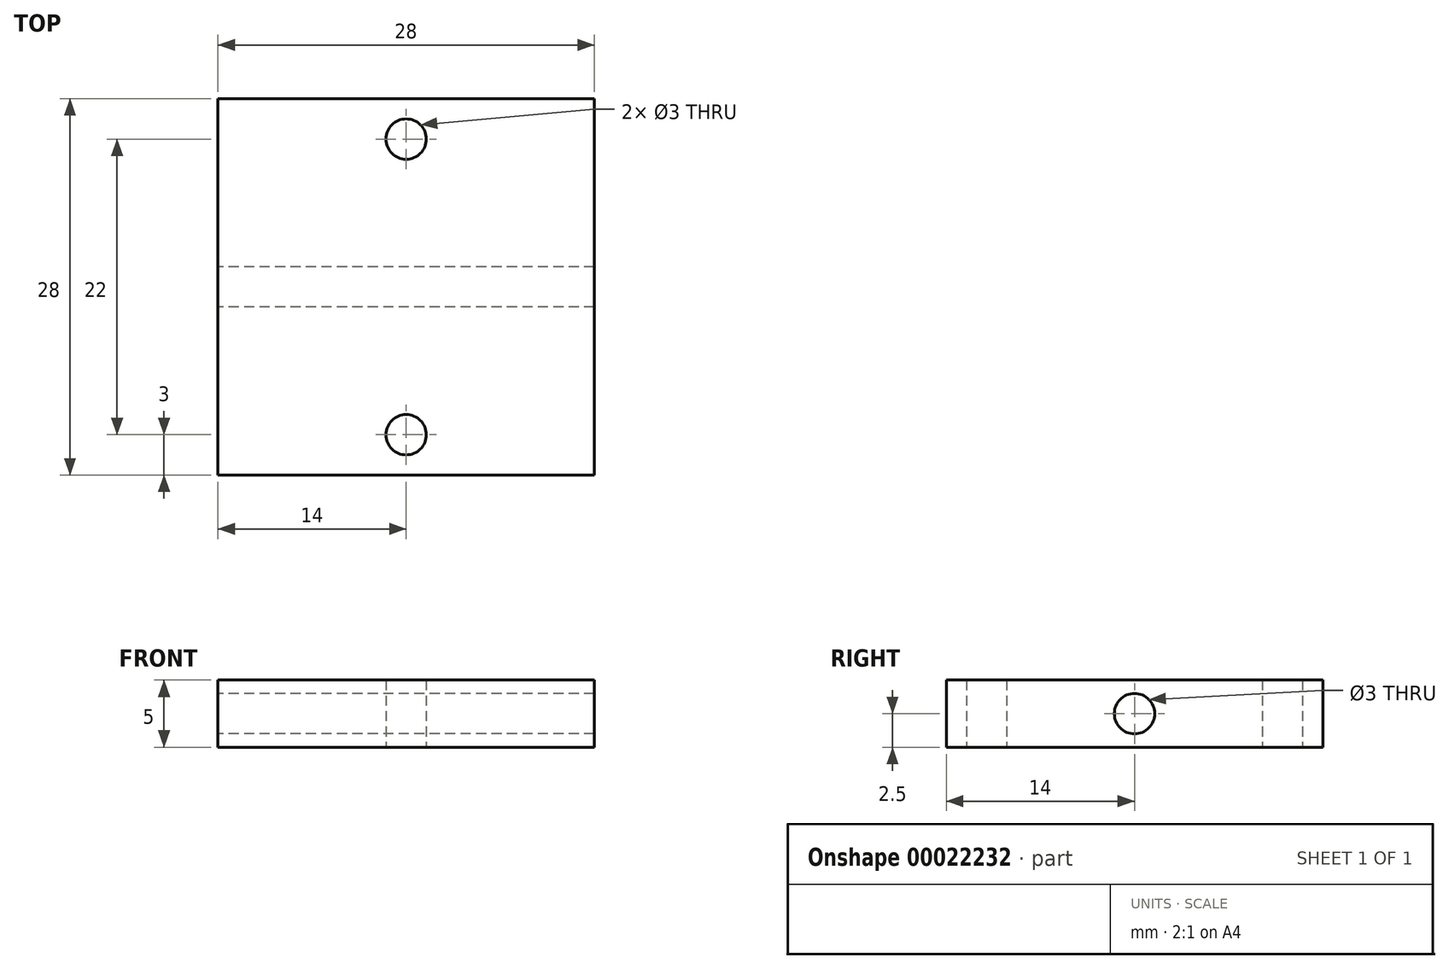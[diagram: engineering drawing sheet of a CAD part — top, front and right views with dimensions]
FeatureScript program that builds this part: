
annotation { "Feature Type Name" : "Feature", "Feature Type Description" : "" }
export const myFeature = defineFeature(function(context is Context, id is Id, definition is map)
    precondition{}
    {
        {
            var Q0;
            Q0=qCreatedBy(makeId("Top.planeOp"),FACE);
            var sketch = newSketch(context, id + "F0", { "sketchPlane" : qUnion([Q0])});
            skLineSegment(sketch, "E0.rect.bottom", {"start": v(14, 14) * mm, "end": v(-14, 14) * mm});
            skLineSegment(sketch, "E0.rect.top", {"start": v(14, -14) * mm, "end": v(-14, -14) * mm});
            skLineSegment(sketch, "E0.rect.left", {"start": v(14, 14) * mm, "end": v(14, -14) * mm});
            skLineSegment(sketch, "E0.rect.right", {"start": v(-14, 14) * mm, "end": v(-14, -14) * mm});
            skPoint(sketch, "E0.rect.middle", {"position": v(0, 0) * mm});
            skCircle(sketch, "E1", {"center": v(0, 11) * mm, "radius": 1.5 * mm});
            skCircle(sketch, "E2", {"center": v(0, -11) * mm, "radius": 1.5 * mm});
            skSolve(sketch);
        }
        {
            var Q0;
            Q0=makeQuery(id+"F0.imprint","IMPRINT",FACE,{"disambiguationData":[TD([[makeQuery(id+"F0.imprint","IMPRINT",EDGE,{"derivedFrom":sQuery(id+"F0.wireOp",EDGE,"E0.rect.bottom")}),1.0]])]});
            extrude(context, id + "F1", {"entities" : qUnion([Q0]), "depth" : 5 * mm});
        }
        {
            var Q0;
            Q0=makeQuery(id+"F1.opExtrude","SWEPT_FACE",FACE,{"disambiguationData":[OSD([sQuery(id+"F0.wireOp",EDGE,"E0.rect.right")])]});
            var sketch = newSketch(context, id + "F2", { "sketchPlane" : qUnion([Q0])});
            skCircle(sketch, "E3", {"center": v(0, 2.5) * mm, "radius": 1.5 * mm});
            skSolve(sketch);
        }
        {
            var Q0;
            Q0=makeQuery(id+"F2.imprint","IMPRINT",FACE,{"disambiguationData":[TD([[makeQuery(id+"F2.imprint","IMPRINT",EDGE,{"derivedFrom":sQuery(id+"F2.wireOp",EDGE,"E3")}),1.0]])]});
            extrude(context, id + "F3", {"entities" : qUnion([Q0]), "operationType" : NewBodyOperationType.REMOVE, "oppositeDirection" : true, "depth" : 29 * mm});
        }
    });
